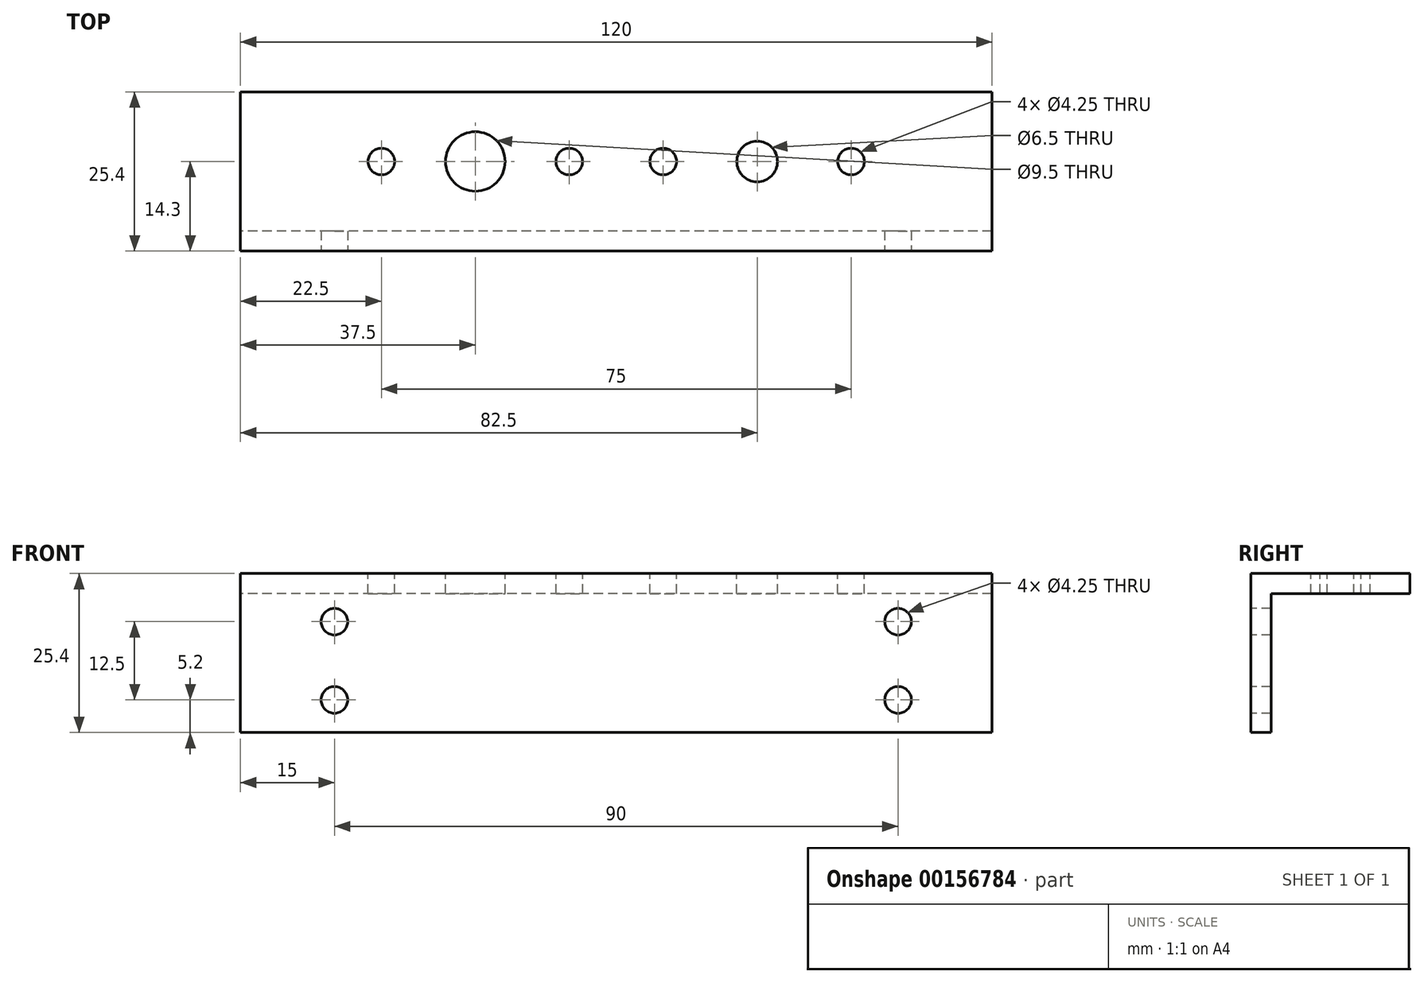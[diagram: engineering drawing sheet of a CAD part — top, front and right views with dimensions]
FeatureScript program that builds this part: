
annotation { "Feature Type Name" : "Feature", "Feature Type Description" : "" }
export const myFeature = defineFeature(function(context is Context, id is Id, definition is map)
    precondition{}
    {
        {
            var Q0;
            Q0=qCreatedBy(makeId("Right.planeOp"),FACE);
            var sketch = newSketch(context, id + "F0", { "sketchPlane" : qUnion([Q0])});
            skLineSegment(sketch, "E0", {"start": v(0, -25.4) * mm, "end": v(-3.2, -25.4) * mm});
            skLineSegment(sketch, "E1", {"start": v(-3.2, -25.4) * mm, "end": v(-3.2, 0) * mm});
            skLineSegment(sketch, "E2", {"start": v(-3.2, 0) * mm, "end": v(22.2, 0) * mm});
            skLineSegment(sketch, "E3", {"start": v(22.2, 0) * mm, "end": v(22.2, -3.2) * mm});
            skLineSegment(sketch, "E4", {"start": v(22.2, -3.2) * mm, "end": v(0, -3.2) * mm});
            skLineSegment(sketch, "E5", {"start": v(0, -3.2) * mm, "end": v(0, -25.4) * mm});
            skSolve(sketch);
        }
        {
            var Q0;
            Q0 = qSketchRegion(id + "F0", true);
            extrude(context, id + "F1", {"entities" : qUnion([Q0]), "endBound" : BoundingType.SYMMETRIC, "depth" : 165 * mm});
        }
        {
            var Q0;
            Q0=makeQuery(id+"F1.opExtrude","SWEPT_FACE",FACE,{"disambiguationData":[OSD([sQuery(id+"F0.wireOp",EDGE,"E1")])]});
            var sketch = newSketch(context, id + "F2", { "sketchPlane" : qUnion([Q0])});
            skCircle(sketch, "E6", {"center": v(-67.5, -20.2) * mm, "radius": 2.12 * mm});
            skCircle(sketch, "E7", {"center": v(-67.5, -7.7) * mm, "radius": 2.12 * mm});
            skLineSegment(sketch, "E8", {"start": v(-82.5, -12.7) * mm, "end": v(82.5, -12.7) * mm, "construction": true});
            skCircle(sketch, "E9.MirrorC", {"center": v(22.5, -7.7) * mm, "radius": 2.12 * mm});
            skCircle(sketch, "E10.MirrorC", {"center": v(22.5, -20.2) * mm, "radius": 2.12 * mm});
            skLineSegment(sketch, "E11.bottom", {"start": v(82.5, 0) * mm, "end": v(37.5, 0) * mm});
            skLineSegment(sketch, "E11.top", {"start": v(82.5, -25.4) * mm, "end": v(37.5, -25.4) * mm});
            skLineSegment(sketch, "E11.left", {"start": v(82.5, 0) * mm, "end": v(82.5, -25.4) * mm});
            skLineSegment(sketch, "E11.right", {"start": v(37.5, 0) * mm, "end": v(37.5, -25.4) * mm});
            skSolve(sketch);
        }
        {
            var Q0;
            Q0 = qSketchRegion(id + "F2", true);
            extrude(context, id + "F3", {"entities" : qUnion([Q0]), "operationType" : NewBodyOperationType.REMOVE, "endBound" : BoundingType.THROUGH_ALL, "oppositeDirection" : true, "depth" : 5 * mm});
        }
        {
            var Q0;
            Q0=makeQuery(id+"F1.opExtrude","SWEPT_FACE",FACE,{"disambiguationData":[OSD([sQuery(id+"F0.wireOp",EDGE,"E2")])]});
            var sketch = newSketch(context, id + "F4", { "sketchPlane" : qUnion([Q0])});
            skCircle(sketch, "E12", {"center": v(0, 11.1) * mm, "radius": 3.25 * mm});
            skCircle(sketch, "E13", {"center": v(-45, 11.1) * mm, "radius": 4.75 * mm});
            skCircle(sketch, "E14", {"center": v(-60, 11.1) * mm, "radius": 2.12 * mm});
            skCircle(sketch, "E15", {"center": v(-30, 11.1) * mm, "radius": 2.12 * mm});
            skCircle(sketch, "E16", {"center": v(-15, 11.1) * mm, "radius": 2.12 * mm});
            skCircle(sketch, "E17.MirrorC", {"center": v(15, 11.1) * mm, "radius": 2.12 * mm});
            skSolve(sketch);
        }
        {
            var Q0;
            Q0 = qSketchRegion(id + "F4", true);
            extrude(context, id + "F5", {"entities" : qUnion([Q0]), "operationType" : NewBodyOperationType.REMOVE, "oppositeDirection" : true, "depth" : 5 * mm});
        }
    });
